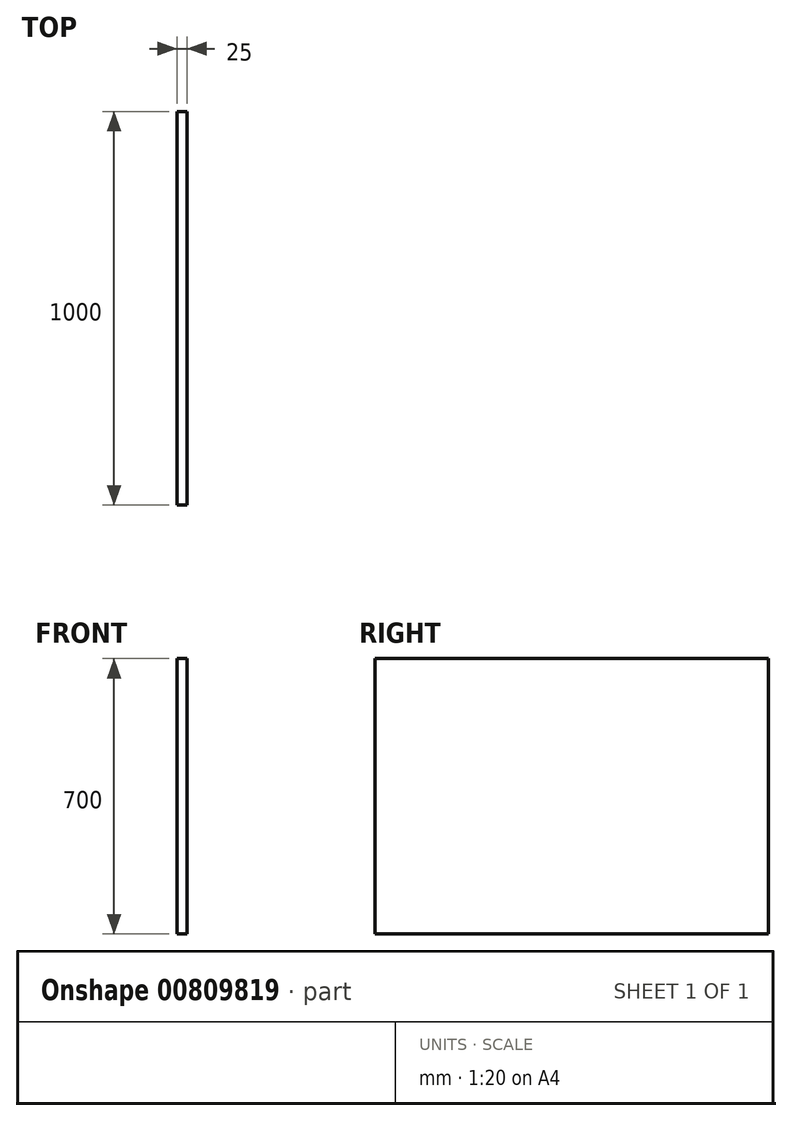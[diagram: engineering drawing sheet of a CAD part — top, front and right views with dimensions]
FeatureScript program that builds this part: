
annotation { "Feature Type Name" : "Feature", "Feature Type Description" : "" }
export const myFeature = defineFeature(function(context is Context, id is Id, definition is map)
    precondition{}
    {
        {
            var Q0;
            Q0=qCreatedBy(makeId("Right.planeOp"),FACE);
            var sketch = newSketch(context, id + "F0", { "sketchPlane" : qUnion([Q0])});
            skLineSegment(sketch, "E0.bottom", {"start": v(-500, 350) * mm, "end": v(500, 350) * mm});
            skLineSegment(sketch, "E0.top", {"start": v(-500, -350) * mm, "end": v(500, -350) * mm});
            skLineSegment(sketch, "E0.left", {"start": v(-500, 350) * mm, "end": v(-500, -350) * mm});
            skLineSegment(sketch, "E0.right", {"start": v(500, 350) * mm, "end": v(500, -350) * mm});
            skSolve(sketch);
        }
        {
            var Q0;
            Q0=makeQuery(id+"F0.imprint","IMPRINT",FACE,{"disambiguationData":[TD([[makeQuery(id+"F0.imprint","IMPRINT",EDGE,{"derivedFrom":sQuery(id+"F0.wireOp",EDGE,"E0.bottom")}),-1.0]])]});
            extrude(context, id + "F1", {"entities" : qUnion([Q0]), "depth" : 25 * mm, "offsetDistance" : 25 * mm});
        }
    });
